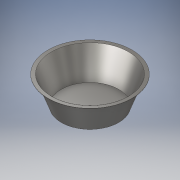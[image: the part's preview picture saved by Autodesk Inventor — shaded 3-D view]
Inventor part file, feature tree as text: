
AUTODESK INVENTOR PART (.ipt)
format: ipt  version: 2018 (Build 220112000, 112)  size: 128,000 bytes
history: native  units: in
note: dims shown in document units (in); Inventor stores cm internally (conversion verified against a paired STEP export)
features: revolve x1, sketch x1
ambient origin geometry x8: Origin, YZ Plane, XZ Plane, XY Plane, X Axis, Y Axis, Z Axis, Center Point
bodies: Solid1 (feature_tree)
feature tree (2):
  revolve  "Revolution1"  [1 undecoded]
  sketch  "Sketch1"  dims[d0=1.5in d1=1.4375in d2=2.25in d5=0.013in d6=90.0deg d7=0.013in d9=90.0deg]
note: 1 required parameter value undecoded (feature->parameter linkage not recoverable at this tier; creation-order binding heuristic only, values carry confidence <= 0.55)
